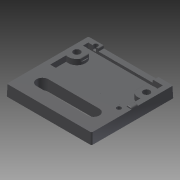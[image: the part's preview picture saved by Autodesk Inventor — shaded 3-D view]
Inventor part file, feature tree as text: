
AUTODESK INVENTOR PART (.ipt)
format: ipt  version: 2013 (Build 170138000, 138)  size: 364,544 bytes
history: native  units: mm (DEFAULTED — no unit token found)
features: imported_body x1, plane x1
ambient origin geometry x8: Origin, YZ Plane, XZ Plane, XY Plane, X Axis, Y Axis, Z Axis, Center Point
bodies: Solid1 (feature_tree)
feature tree (2):
  imported_body  "Base1"
  plane  "Work Plane1"
